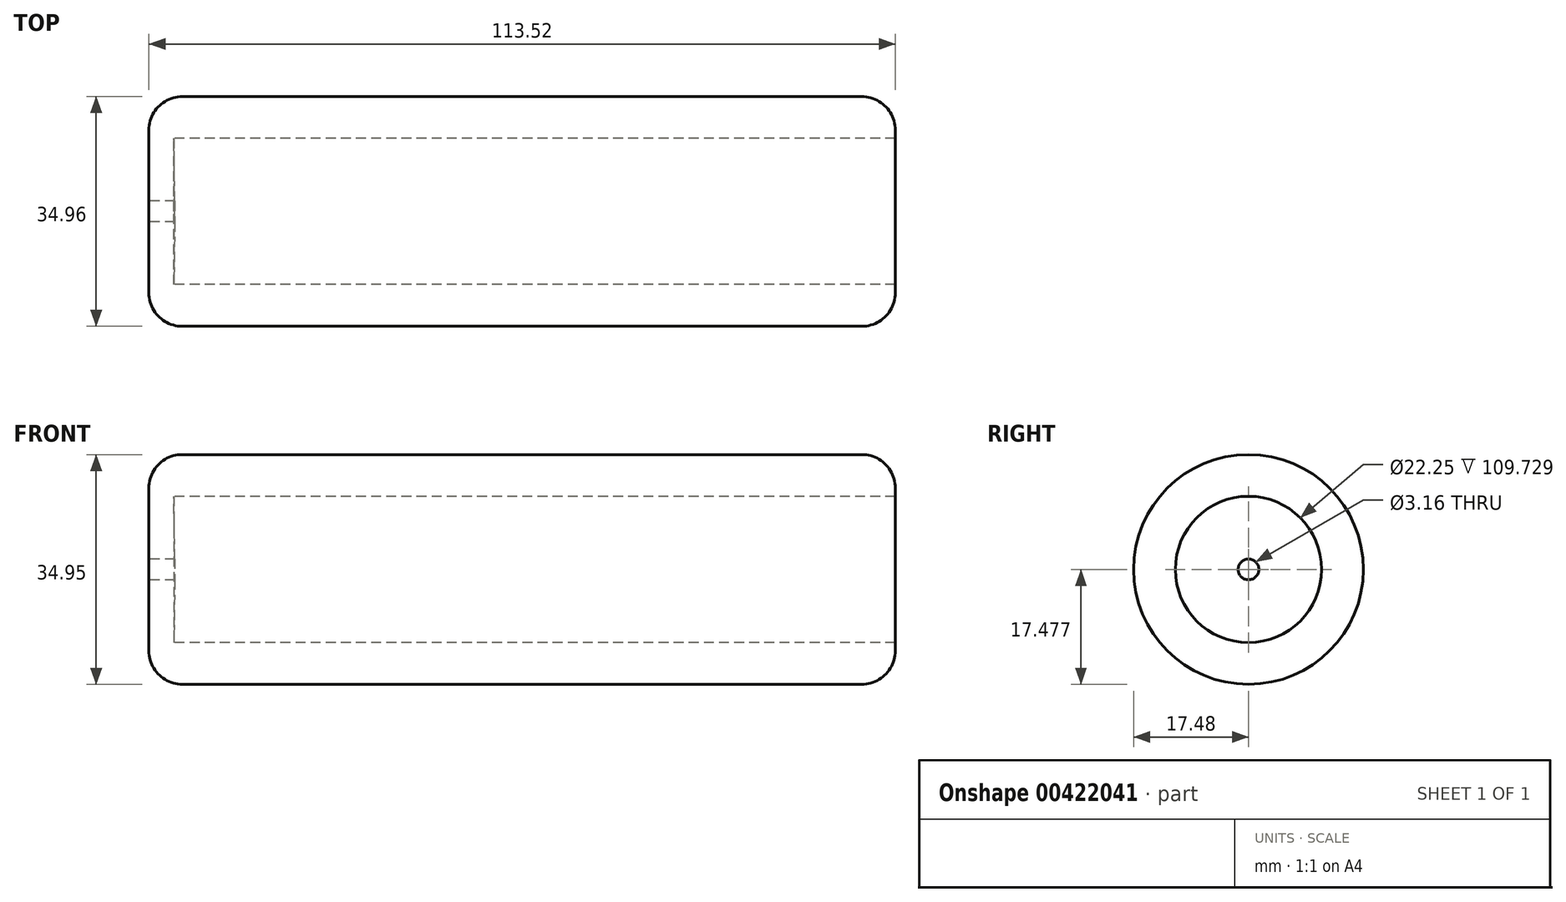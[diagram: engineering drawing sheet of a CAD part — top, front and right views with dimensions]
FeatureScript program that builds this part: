
annotation { "Feature Type Name" : "Feature", "Feature Type Description" : "" }
export const myFeature = defineFeature(function(context is Context, id is Id, definition is map)
    precondition{}
    {
        {
            var Q0;
            Q0=qCreatedBy(makeId("Front.planeOp"),FACE);
            var sketch = newSketch(context, id + "F0", { "sketchPlane" : qUnion([Q0])});
            skLineSegment(sketch, "E0", {"start": v(-55.66, -22.04) * mm, "end": v(57.86, -22.04) * mm});
            skLineSegment(sketch, "E1", {"start": v(57.86, -22.04) * mm, "end": v(57.86, -15.69) * mm});
            skLineSegment(sketch, "E2", {"start": v(-55.66, -22.04) * mm, "end": v(-55.66, -4.56) * mm});
            skLineSegment(sketch, "E3", {"start": v(-55.66, -4.56) * mm, "end": v(-51.7, -4.56) * mm});
            skLineSegment(sketch, "E4", {"start": v(57.86, -15.69) * mm, "end": v(-51.87, -15.69) * mm});
            skLineSegment(sketch, "E5", {"start": v(-51.87, -15.69) * mm, "end": v(-51.7, -4.56) * mm});
            skSolve(sketch);
        }
        {
            var Q0;
            Q0=makeQuery(id+"F0.imprint","IMPRINT",FACE,{"disambiguationData":[TD([[makeQuery(id+"F0.imprint","IMPRINT",EDGE,{"derivedFrom":sQuery(id+"F0.wireOp",EDGE,"E0")}),1.0]])]});
            var Q1;
            Q1=sQuery(id+"F0.wireOp",EDGE,"E3");
            revolve(context, id + "F1", {"entities" : qUnion([Q0]), "axis" : qUnion([Q1]), "revolveType" : RevolveType.FULL});
        }
        {
            var Q0;
            Q0=makeQuery(id+"F1.opRevolve","SWEPT_EDGE",EDGE,{"disambiguationData":[OSD([sQuery(id+"F0.wireOp",EDGE,"E0"),sQuery(id+"F0.wireOp",EDGE,"E1")])]});
            var Q1;
            Q1=makeQuery(id+"F1.opRevolve","SWEPT_EDGE",EDGE,{"disambiguationData":[OSD([sQuery(id+"F0.wireOp",EDGE,"E0"),sQuery(id+"F0.wireOp",EDGE,"E2")])]});
            fillet(context, id + "F2", {"entities" : qUnion([Q0, Q1]), "radius" : 5.08 * mm, "tangentPropagation" : true, "allowEdgeOverflow" : false});
        }
        {
            var Q0;
            Q0=makeQuery(id+"F1.opRevolve","SWEPT_FACE",FACE,{"disambiguationData":[OSD([sQuery(id+"F0.wireOp",EDGE,"E2")])]});
            var sketch = newSketch(context, id + "F3", { "sketchPlane" : qUnion([Q0])});
            skCircle(sketch, "E6", {"center": v(0, -4.56) * mm, "radius": 1.58 * mm});
            skSolve(sketch);
        }
        {
            var Q0;
            Q0=makeQuery(id+"F3.imprint","IMPRINT",FACE,{"disambiguationData":[TD([[makeQuery(id+"F3.imprint","IMPRINT",EDGE,{"derivedFrom":sQuery(id+"F3.wireOp",EDGE,"E6")}),1.0]])]});
            extrude(context, id + "F4", {"entities" : qUnion([Q0]), "operationType" : NewBodyOperationType.REMOVE, "oppositeDirection" : true, "depth" : 25.4 * mm});
        }
    });
